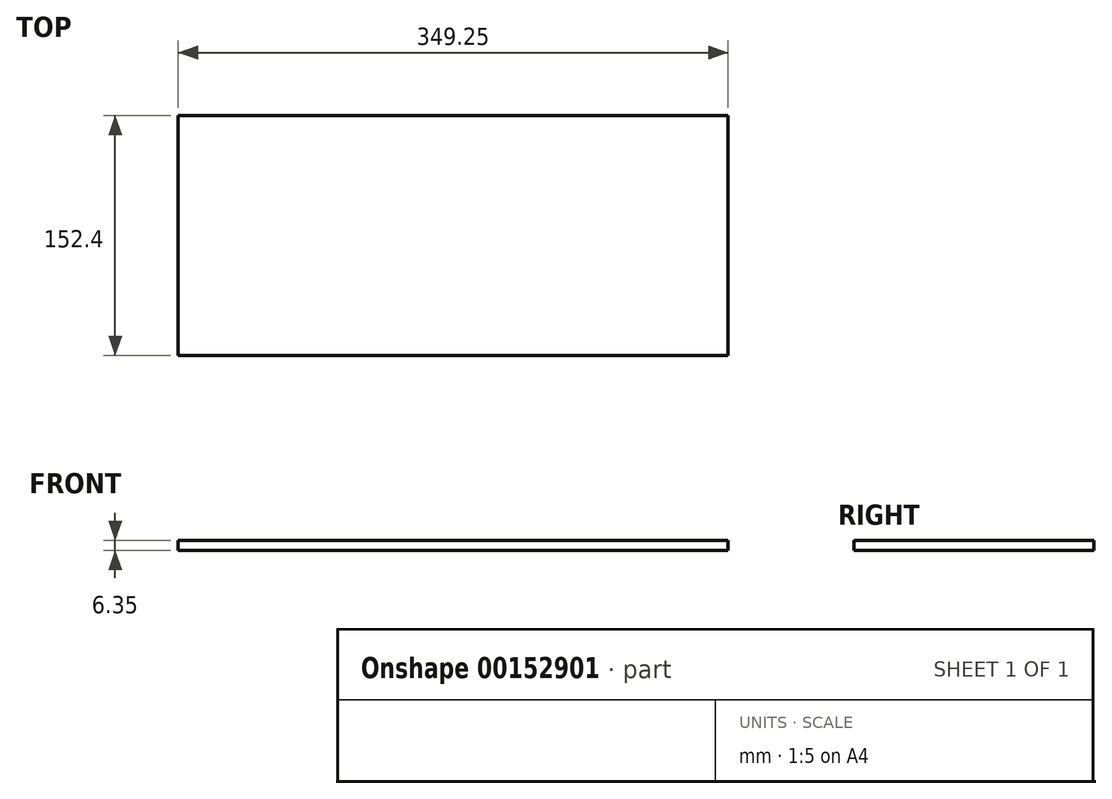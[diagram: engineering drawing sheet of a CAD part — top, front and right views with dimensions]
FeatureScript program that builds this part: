
annotation { "Feature Type Name" : "Feature", "Feature Type Description" : "" }
export const myFeature = defineFeature(function(context is Context, id is Id, definition is map)
    precondition{}
    {
        {
            var Q0;
            Q0=qCreatedBy(makeId("Top.planeOp"),FACE);
            var sketch = newSketch(context, id + "F0", { "sketchPlane" : qUnion([Q0])});
            skLineSegment(sketch, "E0.bottom", {"start": v(0, 0) * mm, "end": v(349.25, 0) * mm});
            skLineSegment(sketch, "E0.top", {"start": v(0, -152.4) * mm, "end": v(349.25, -152.4) * mm});
            skLineSegment(sketch, "E0.left", {"start": v(0, 0) * mm, "end": v(0, -152.4) * mm});
            skLineSegment(sketch, "E0.right", {"start": v(349.25, 0) * mm, "end": v(349.25, -152.4) * mm});
            skSolve(sketch);
        }
        {
            var Q0;
            Q0=qSketchRegion(id+"F0",true);
            extrude(context, id + "F1", {"entities" : qUnion([Q0]), "depth" : 6.35 * mm});
        }
    });
